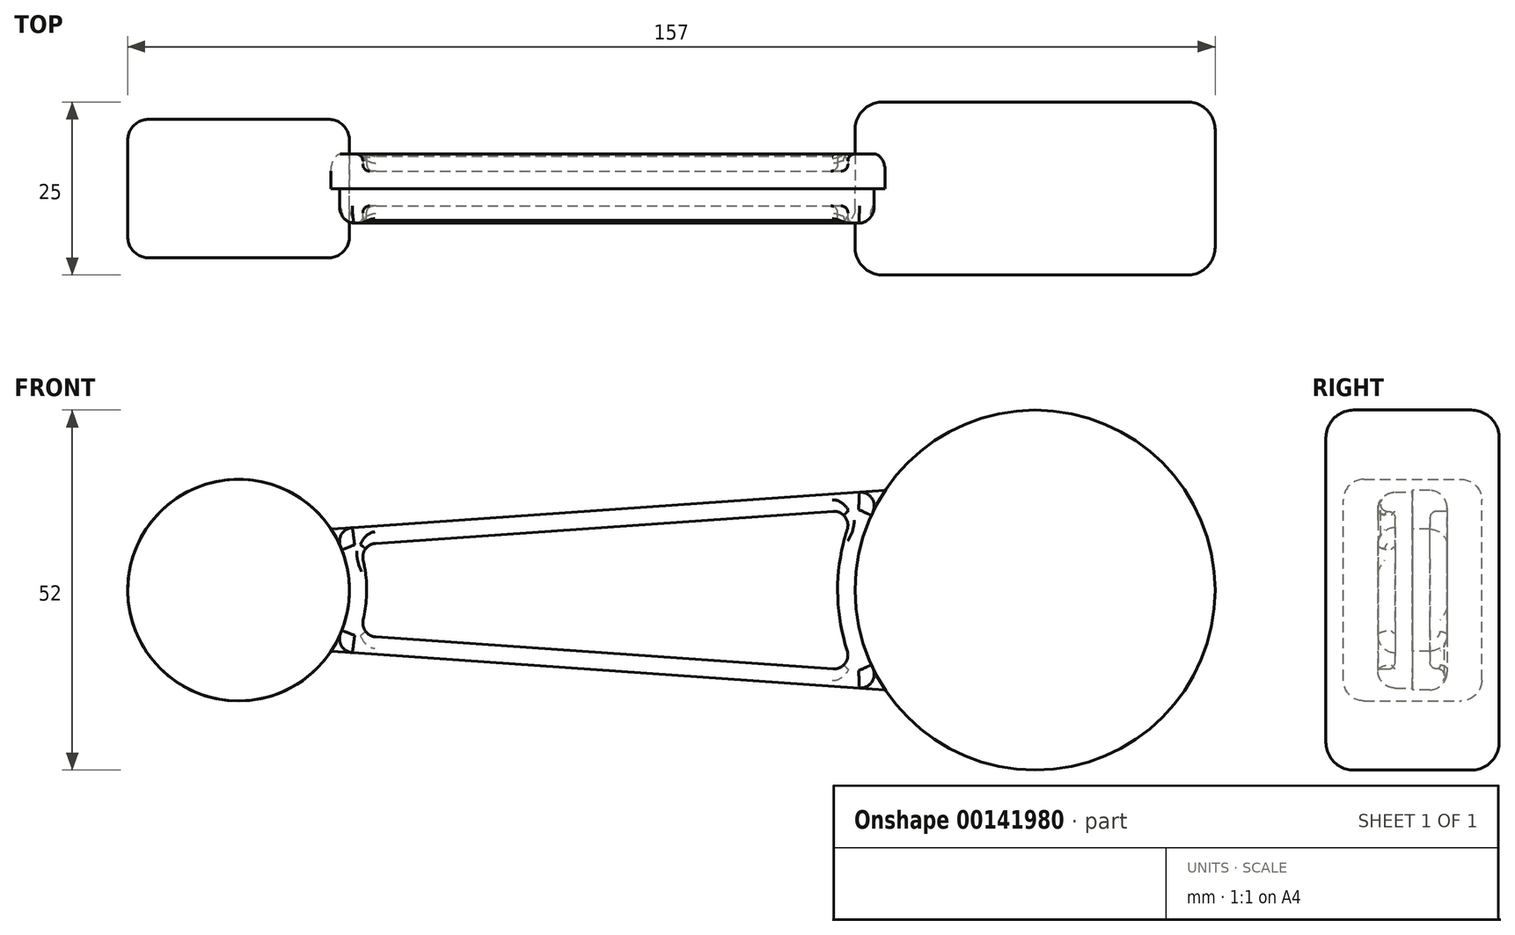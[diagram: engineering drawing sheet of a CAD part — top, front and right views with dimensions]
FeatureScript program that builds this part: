
annotation { "Feature Type Name" : "Feature", "Feature Type Description" : "" }
export const myFeature = defineFeature(function(context is Context, id is Id, definition is map)
    precondition{}
    {
        {
            var Q0;
            Q0=qCreatedBy(makeId("Front.planeOp"),FACE);
            var sketch = newSketch(context, id + "F0", { "sketchPlane" : qUnion([Q0])});
            skCircle(sketch, "E0", {"center": v(0, 0) * mm, "radius": 26 * mm});
            skSolve(sketch);
        }
        {
            var Q0;
            Q0 = qSketchRegion(id + "F0", true);
            extrude(context, id + "F1", {"entities" : qUnion([Q0]), "endBound" : BoundingType.SYMMETRIC, "depth" : 25 * mm});
        }
        {
            var Q0;
            Q0=qCreatedBy(makeId("Front.planeOp"),FACE);
            var sketch = newSketch(context, id + "F2", { "sketchPlane" : qUnion([Q0])});
            skCircle(sketch, "E1", {"center": v(-115, 0) * mm, "radius": 16 * mm});
            skSolve(sketch);
        }
        {
            var Q0;
            Q0 = qSketchRegion(id + "F2", true);
            extrude(context, id + "F3", {"entities" : qUnion([Q0]), "endBound" : BoundingType.SYMMETRIC, "depth" : 20 * mm});
        }
        {
            var Q0;
            Q0=qCreatedBy(makeId("Front.planeOp"),FACE);
            var sketch = newSketch(context, id + "F4", { "sketchPlane" : qUnion([Q0])});
            skLineSegment(sketch, "E2", {"start": v(0, 0) * mm, "end": v(-117.18, 0) * mm, "construction": true});
            skLineSegment(sketch, "E3", {"start": v(-101.64, 8.81) * mm, "end": v(-21.64, 14.4) * mm});
            skLineSegment(sketch, "E4", {"start": v(-101.64, -8.81) * mm, "end": v(-21.64, -14.4) * mm});
            skArc(sketch, "E5.0", {"start": v(-101.64, -8.81) * mm, "mid": v(-99, 0) * mm, "end": v(-101.64, 8.81) * mm});
            skArc(sketch, "E6.0", {"start": v(-21.64, 14.4) * mm, "mid": v(-26, 0) * mm, "end": v(-21.64, -14.4) * mm});
            skSolve(sketch);
        }
        {
            var Q0;
            Q0 = qSketchRegion(id + "F4", true);
            extrude(context, id + "F5", {"entities" : qUnion([Q0]), "depth" : 5 * mm});
        }
        {
            var Q0;
            Q0=makeQuery(id+"F5.opExtrude","CAP_FACE",FACE,{"disambiguationData":[OSD([sQuery(id+"F4.wireOp",EDGE,"E3"),sQuery(id+"F4.wireOp",EDGE,"E4"),sQuery(id+"F4.wireOp",EDGE,"E5.0"),sQuery(id+"F4.wireOp",EDGE,"E6.0")])],"isStart":false});
            shell(context, id + "F6", {"entities" : qUnion([Q0]), "thickness" : 2.5 * mm});
        }
        {
            var Q0;
            Q0=makeQuery(id+"F5.opExtrude","SWEPT_BODY",BODY,{"disambiguationData":[OSD([sQuery(id+"F4.wireOp",EDGE,"E3"),sQuery(id+"F4.wireOp",EDGE,"E4"),sQuery(id+"F4.wireOp",EDGE,"E5.0"),sQuery(id+"F4.wireOp",EDGE,"E6.0")])]});
            var Q1;
            Q1=makeQuery(id+"F5.opExtrude","CAP_FACE",FACE,{"disambiguationData":[OSD([sQuery(id+"F4.wireOp",EDGE,"E3"),sQuery(id+"F4.wireOp",EDGE,"E4"),sQuery(id+"F4.wireOp",EDGE,"E5.0"),sQuery(id+"F4.wireOp",EDGE,"E6.0")])],"isStart":true});
            mirror(context, id + "F7", {"entities" : qUnion([Q0]), "mirrorPlane" : qUnion([Q1])});
        }
        {
            var Q0;
            Q0=makeQuery(id+"F7.opPattern","COPY",EDGE,{"derivedFrom":makeQuery(id+"F6.opShell","OFFSET_EDGE",EDGE,{"disambiguationData":[OSD([sQuery(id+"F4.wireOp",EDGE,"E3"),sQuery(id+"F4.wireOp",EDGE,"E6.0")])]}),"instanceName":"1"});
            var Q1;
            Q1=makeQuery(id+"F7.opPattern","COPY",EDGE,{"derivedFrom":makeQuery(id+"F6.opShell","OFFSET_EDGE",EDGE,{"disambiguationData":[OSD([sQuery(id+"F4.wireOp",EDGE,"E4"),sQuery(id+"F4.wireOp",EDGE,"E6.0")])]}),"instanceName":"1"});
            var Q2;
            Q2=makeQuery(id+"F7.opPattern","COPY",EDGE,{"derivedFrom":makeQuery(id+"F6.opShell","OFFSET_EDGE",EDGE,{"disambiguationData":[OSD([sQuery(id+"F4.wireOp",EDGE,"E3"),sQuery(id+"F4.wireOp",EDGE,"E5.0")])]}),"instanceName":"1"});
            var Q3;
            Q3=makeQuery(id+"F7.opPattern","COPY",EDGE,{"derivedFrom":makeQuery(id+"F6.opShell","OFFSET_EDGE",EDGE,{"disambiguationData":[OSD([sQuery(id+"F4.wireOp",EDGE,"E4"),sQuery(id+"F4.wireOp",EDGE,"E5.0")])]}),"instanceName":"1"});
            var Q4;
            Q4=makeQuery(id+"F6.opShell","OFFSET_EDGE",EDGE,{"disambiguationData":[OSD([sQuery(id+"F4.wireOp",EDGE,"E3"),sQuery(id+"F4.wireOp",EDGE,"E5.0")])]});
            var Q5;
            Q5=makeQuery(id+"F6.opShell","OFFSET_EDGE",EDGE,{"disambiguationData":[OSD([sQuery(id+"F4.wireOp",EDGE,"E4"),sQuery(id+"F4.wireOp",EDGE,"E5.0")])]});
            var Q6;
            Q6=makeQuery(id+"F6.opShell","OFFSET_EDGE",EDGE,{"disambiguationData":[OSD([sQuery(id+"F4.wireOp",EDGE,"E3"),sQuery(id+"F4.wireOp",EDGE,"E6.0")])]});
            var Q7;
            Q7=makeQuery(id+"F6.opShell","OFFSET_EDGE",EDGE,{"disambiguationData":[OSD([sQuery(id+"F4.wireOp",EDGE,"E4"),sQuery(id+"F4.wireOp",EDGE,"E6.0")])]});
            fillet(context, id + "F8", {"entities" : qUnion([Q0, Q1, Q2, Q3, Q4, Q5, Q6, Q7]), "radius" : 2 * mm, "tangentPropagation" : true, "allowEdgeOverflow" : false});
        }
        {
            var Q0;
            {var subQ0=sQuery(id+"F4.wireOp",EDGE,"E3");Q0=makeQuery(id+"F6.opShell","OFFSET_EDGE",EDGE,{"disambiguationData":[OSD([subQ0]),TDD([makeQuery(id+"F5.opExtrude","CAP_EDGE",EDGE,{"disambiguationData":[OSD([subQ0])],"isStart":true})])]});}
            var Q1;
            {var subQ0=sQuery(id+"F4.wireOp",EDGE,"E4");Q1=makeQuery(id+"F7.opPattern","COPY",EDGE,{"derivedFrom":makeQuery(id+"F6.opShell","OFFSET_EDGE",EDGE,{"disambiguationData":[OSD([subQ0]),TDD([makeQuery(id+"F5.opExtrude","CAP_EDGE",EDGE,{"disambiguationData":[OSD([subQ0])],"isStart":true})])]}),"instanceName":"1"});}
            fillet(context, id + "F9", {"entities" : qUnion([Q0, Q1]), "radius" : 1 * mm, "tangentPropagation" : true, "allowEdgeOverflow" : false});
        }
        {
            var Q0;
            Q0=makeQuery(id+"F7.opPattern","COPY",EDGE,{"derivedFrom":makeQuery(id+"F5.opExtrude","CAP_EDGE",EDGE,{"disambiguationData":[OSD([sQuery(id+"F4.wireOp",EDGE,"E3")])],"isStart":false}),"instanceName":"1"});
            var Q1;
            Q1=makeQuery(id+"F5.opExtrude","CAP_EDGE",EDGE,{"disambiguationData":[OSD([sQuery(id+"F4.wireOp",EDGE,"E3")])],"isStart":false});
            var Q2;
            Q2=makeQuery(id+"F5.opExtrude","CAP_EDGE",EDGE,{"disambiguationData":[OSD([sQuery(id+"F4.wireOp",EDGE,"E4")])],"isStart":false});
            var Q3;
            Q3=makeQuery(id+"F7.opPattern","COPY",EDGE,{"derivedFrom":makeQuery(id+"F5.opExtrude","CAP_EDGE",EDGE,{"disambiguationData":[OSD([sQuery(id+"F4.wireOp",EDGE,"E4")])],"isStart":false}),"instanceName":"1"});
            fillet(context, id + "F10", {"entities" : qUnion([Q0, Q1, Q2, Q3]), "radius" : 2.5 * mm, "tangentPropagation" : true, "allowEdgeOverflow" : false});
        }
        {
            var Q0;
            Q0=makeQuery(id+"F5.opExtrude","CAP_EDGE",EDGE,{"disambiguationData":[OSD([sQuery(id+"F4.wireOp",EDGE,"E5.0")])],"isStart":false});
            fillet(context, id + "F11", {"entities" : qUnion([Q0]), "radius" : 2 * mm, "tangentPropagation" : true, "allowEdgeOverflow" : false});
        }
        {
            var Q0;
            Q0=makeQuery(id+"F5.opExtrude","CAP_EDGE",EDGE,{"disambiguationData":[OSD([sQuery(id+"F4.wireOp",EDGE,"E6.0")])],"isStart":false});
            fillet(context, id + "F12", {"entities" : qUnion([Q0]), "radius" : 2 * mm, "tangentPropagation" : true, "allowEdgeOverflow" : false});
        }
        {
            var Q0;
            {var subQ0=sQuery(id+"F4.wireOp",EDGE,"E3");Q0=makeQuery(id+"F10.opFillet","BLEND_EDGE",EDGE,{"blendedFrom":[makeQuery(id+"F5.opExtrude","CAP_EDGE",EDGE,{"disambiguationData":[OSD([subQ0])],"isStart":false}),makeQuery(id+"F6.opShell","OFFSET_FACE",FACE,{"disambiguationData":[OSD([subQ0])]})],"blendedInto":[makeQuery(id+"F6.opShell","OFFSET_FACE",FACE,{"disambiguationData":[OSD([subQ0])]})]});}
            var Q1;
            {var subQ0=sQuery(id+"F4.wireOp",EDGE,"E4");Q1=makeQuery(id+"F10.opFillet","BLEND_EDGE",EDGE,{"blendedFrom":[makeQuery(id+"F7.opPattern","COPY",EDGE,{"derivedFrom":makeQuery(id+"F5.opExtrude","CAP_EDGE",EDGE,{"disambiguationData":[OSD([subQ0])],"isStart":false}),"instanceName":"1"}),makeQuery(id+"F7.opPattern","COPY",FACE,{"derivedFrom":makeQuery(id+"F6.opShell","OFFSET_FACE",FACE,{"disambiguationData":[OSD([subQ0])]}),"instanceName":"1"})],"blendedInto":[makeQuery(id+"F7.opPattern","COPY",FACE,{"derivedFrom":makeQuery(id+"F6.opShell","OFFSET_FACE",FACE,{"disambiguationData":[OSD([subQ0])]}),"instanceName":"1"})]});}
            fillet(context, id + "F13", {"entities" : qUnion([Q0, Q1]), "radius" : 1 * mm, "tangentPropagation" : true, "allowEdgeOverflow" : false});
        }
        {
            var Q0;
            Q0=makeQuery(id+"F3.opExtrude","CAP_EDGE",EDGE,{"disambiguationData":[OSD([sQuery(id+"F2.wireOp",EDGE,"E1")])],"isStart":true});
            var Q1;
            Q1=makeQuery(id+"F3.opExtrude","CAP_EDGE",EDGE,{"disambiguationData":[OSD([sQuery(id+"F2.wireOp",EDGE,"E1")])],"isStart":false});
            fillet(context, id + "F14", {"entities" : qUnion([Q0, Q1]), "radius" : 3 * mm, "tangentPropagation" : true, "allowEdgeOverflow" : false});
        }
        {
            var Q0;
            Q0=makeQuery(id+"F1.opExtrude","CAP_EDGE",EDGE,{"disambiguationData":[OSD([sQuery(id+"F0.wireOp",EDGE,"E0")])],"isStart":false});
            var Q1;
            Q1=makeQuery(id+"F1.opExtrude","CAP_EDGE",EDGE,{"disambiguationData":[OSD([sQuery(id+"F0.wireOp",EDGE,"E0")])],"isStart":true});
            fillet(context, id + "F15", {"entities" : qUnion([Q0, Q1]), "radius" : 4 * mm, "tangentPropagation" : true, "allowEdgeOverflow" : false});
        }
        {
            var Q0;
            Q0=makeQuery(id+"F3.opExtrude","CAP_FACE",FACE,{"disambiguationData":[OSD([sQuery(id+"F2.wireOp",EDGE,"E1")])],"isStart":true});
            var sketch = newSketch(context, id + "F16", { "sketchPlane" : qUnion([Q0])});
            skPoint(sketch, "E7", {"position": v(115, 0) * mm});
            skSolve(sketch);
        }
        {
            var Q0;
            Q0=makeQuery(id+"F1.opExtrude","CAP_FACE",FACE,{"disambiguationData":[OSD([sQuery(id+"F0.wireOp",EDGE,"E0")])],"isStart":true});
            var sketch = newSketch(context, id + "F17", { "sketchPlane" : qUnion([Q0])});
            skPoint(sketch, "E8", {"position": v(0, 0) * mm});
            skSolve(sketch);
        }
        {
            var Q0;
            Q0=sQuery(id+"F16.wireOp",VERTEX,"E7");
            var Q1;
            Q1=makeQuery(id+"F7.opPattern","COPY",BODY,{"derivedFrom":makeQuery(id+"F5.opExtrude","SWEPT_BODY",BODY,{"disambiguationData":[OSD([sQuery(id+"F4.wireOp",EDGE,"E3"),sQuery(id+"F4.wireOp",EDGE,"E4"),sQuery(id+"F4.wireOp",EDGE,"E5.0"),sQuery(id+"F4.wireOp",EDGE,"E6.0")])]}),"instanceName":"1"});
            hole(context, id + "F18", {"style" : HoleStyle.SIMPLE, "endStyle" : HoleEndStyle.THROUGH, "standardTappedOrClearance" : lookupTablePath({ "standard" : "ISO", "size" : "20", "type" : "Drilled" }), "standardBlindInLast" : lookupTablePath({ "standard" : "ISO", "size" : "20", "type" : "Drilled" }), "holeDiameter" : 20 * mm, "locations" : qUnion([Q0]), "scope" : qUnion([Q1]), "isTappedThrough" : true});
        }
        {
            var Q0;
            Q0=sQuery(id+"F17.wireOp",VERTEX,"E8");
            var Q1;
            Q1=makeQuery(id+"F7.opPattern","COPY",BODY,{"derivedFrom":makeQuery(id+"F5.opExtrude","SWEPT_BODY",BODY,{"disambiguationData":[OSD([sQuery(id+"F4.wireOp",EDGE,"E3"),sQuery(id+"F4.wireOp",EDGE,"E4"),sQuery(id+"F4.wireOp",EDGE,"E5.0"),sQuery(id+"F4.wireOp",EDGE,"E6.0")])]}),"instanceName":"1"});
            hole(context, id + "F19", {"style" : HoleStyle.SIMPLE, "endStyle" : HoleEndStyle.THROUGH, "standardTappedOrClearance" : lookupTablePath({ "standard" : "ISO", "size" : "38", "type" : "Drilled" }), "standardBlindInLast" : lookupTablePath({ "standard" : "ISO", "size" : "38", "type" : "Drilled" }), "holeDiameter" : 38 * mm, "locations" : qUnion([Q0]), "scope" : qUnion([Q1]), "isTappedThrough" : true});
        }
    });
